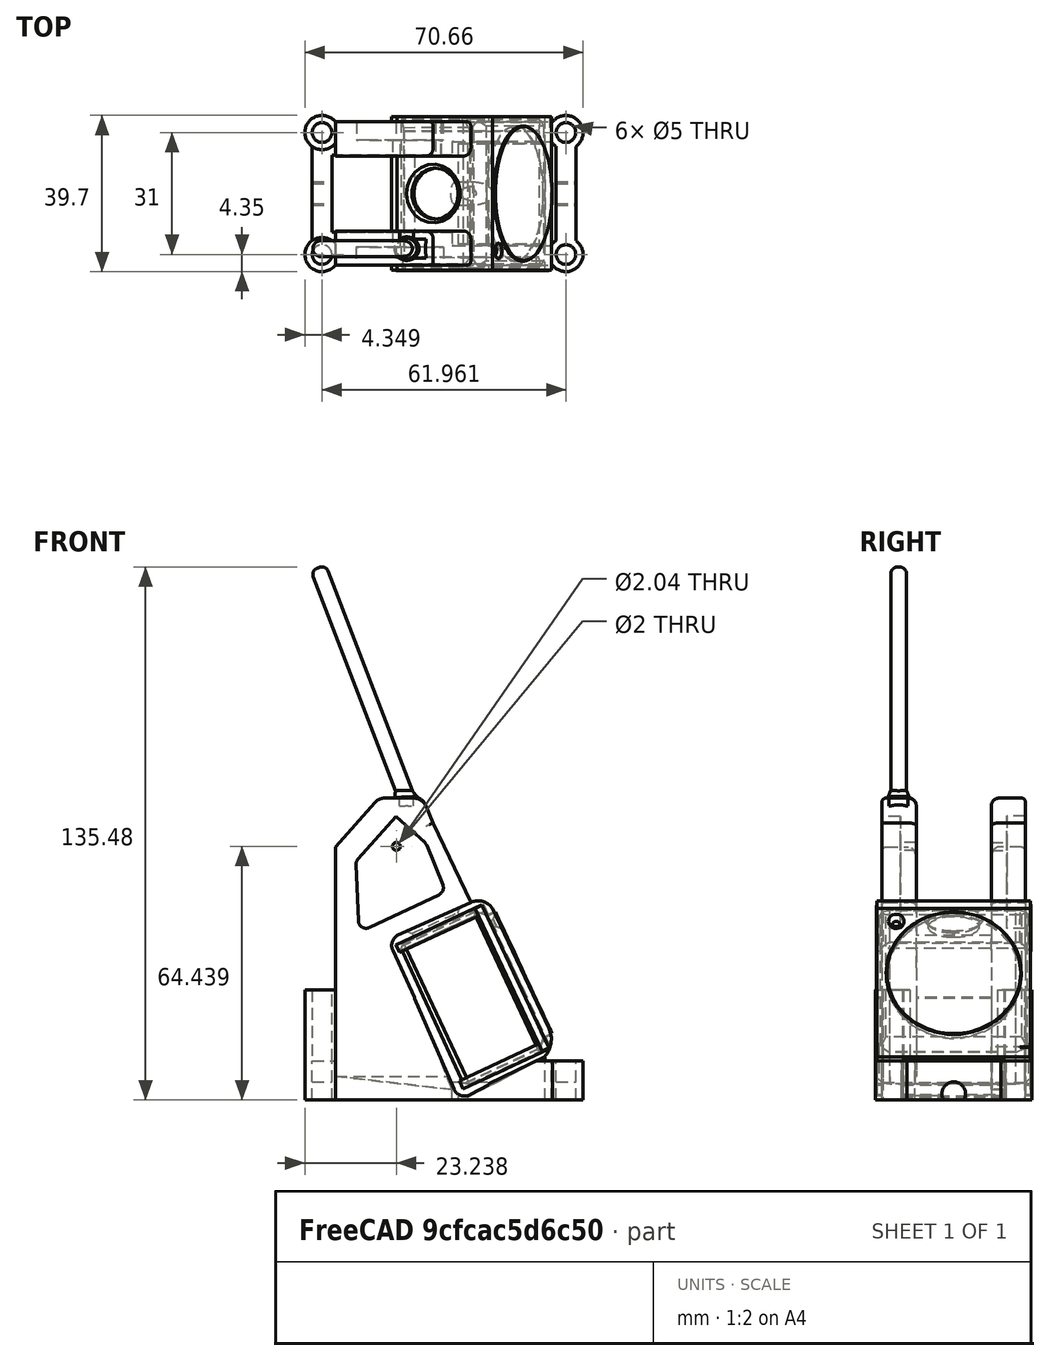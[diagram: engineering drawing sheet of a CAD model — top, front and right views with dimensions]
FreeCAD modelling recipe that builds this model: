
FCSTD DOCUMENT  (FreeCAD 0.19R24267 +99 (Git))
Label: fr7狗坐
License: All rights reserved
LicenseURL: http://en.wikipedia.org/wiki/All_rights_reserved
objects: Sketcher::SketchObject×14, PartDesign::Pad×10, Part::Fillet×6, Part::Cylinder×4, PartDesign::Pocket×4, Part::Cut×4, PartDesign::Body×4, Part::Chamfer×3, Part::Box×3, Part::MultiFuse×3, Mesh::Feature×2, PartDesign::Chamfer×1, Part::Fuse×1, App::MeasureDistance×1
note: 72 computed .brp shape members not serialized (recipe doc carries the construction recipe); baked Part::Feature solids carry a one-line shape summary decoded from their .brp

FEATURE [Sketcher::SketchObject] Sketch
  FullyConstrained = false
  MapMode = 5
  Support = -> [XY_Plane]
  sketch-geometry (30):
    g0: Circle CenterX=-30.9806 CenterY=15.5 CenterZ=0 NormalX=0 NormalY=0 NormalZ=1 AngleXU=0 Radius=2.5
    g1: Circle CenterX=-30.9806 CenterY=-15.5 CenterZ=0 NormalX=0 NormalY=0 NormalZ=1 AngleXU=0 Radius=2.5
    g2: LineSegment StartX=-30.9806 StartY=15.5 StartZ=0 EndX=-30.9806 EndY=-15.5 EndZ=0
    g3: ArcOfCircle CenterX=-30.9806 CenterY=15.5 CenterZ=0 NormalX=0 NormalY=0 NormalZ=1 AngleXU=0 Radius=4.35 StartAngle=5.32464 EndAngle=5.73271
    g4: ArcOfCircle CenterX=-30.9806 CenterY=-15.5 CenterZ=0 NormalX=0 NormalY=0 NormalZ=1 AngleXU=0 Radius=4.35 StartAngle=2.18305 EndAngle=5.60634
    g5: LineSegment StartX=-33.4806 StartY=11.9402 StartZ=0 EndX=-33.4806 EndY=-11.9402 EndZ=0
    g6: LineSegment StartX=-28.4806 StartY=11.9402 StartZ=0 EndX=-28.4806 EndY=-11.9402 EndZ=0
    g7: GeomPoint X=0.092343 Y=18.2246 Z=0
    g8: GeomPoint X=0 Y=13.2246 Z=0
    g9: LineSegment StartX=0.092343 StartY=18.2246 StartZ=0 EndX=-27.5895 EndY=18.2246 EndZ=0
    g10: LineSegment StartX=0 StartY=13.2246 StartZ=0 EndX=-27.2732 EndY=13.2246 EndZ=0
    g11: LineSegment StartX=-0.092343 StartY=-18.2246 StartZ=0 EndX=-27.5895 EndY=-18.2246 EndZ=0
    g12: LineSegment StartX=0 StartY=-13.2246 StartZ=0 EndX=-27.2732 EndY=-13.2246 EndZ=0
    g13: ArcOfCircle CenterX=-30.9806 CenterY=15.5 CenterZ=0 NormalX=0 NormalY=0 NormalZ=1 AngleXU=0 Radius=4.35 StartAngle=0.676845 EndAngle=4.10014
    g14: ArcOfCircle CenterX=-30.9806 CenterY=-15.5 CenterZ=0 NormalX=0 NormalY=0 NormalZ=1 AngleXU=0 Radius=4.35 StartAngle=0.550471 EndAngle=0.958543
    g15: Circle CenterX=30.9806 CenterY=15.5 CenterZ=0 NormalX=0 NormalY=0 NormalZ=1 AngleXU=0 Radius=2.5
    g16: Circle CenterX=30.9806 CenterY=-15.5 CenterZ=0 NormalX=0 NormalY=0 NormalZ=1 AngleXU=0 Radius=2.5
    g17: LineSegment StartX=30.9806 StartY=15.5 StartZ=0 EndX=30.9806 EndY=-15.5 EndZ=0
    g18: ArcOfCircle CenterX=30.9806 CenterY=15.5 CenterZ=0 NormalX=0 NormalY=0 NormalZ=1 AngleXU=0 Radius=4.35 StartAngle=3.69206 EndAngle=4.10014
    g19: ArcOfCircle CenterX=30.9806 CenterY=-15.5 CenterZ=0 NormalX=0 NormalY=0 NormalZ=1 AngleXU=0 Radius=4.35 StartAngle=3.81844 EndAngle=7.24173
    g20: LineSegment StartX=33.4806 StartY=11.9402 StartZ=0 EndX=33.4806 EndY=-11.9402 EndZ=0
    g21: LineSegment StartX=28.4806 StartY=11.9402 StartZ=0 EndX=28.4806 EndY=-11.9402 EndZ=0
    g22: GeomPoint X=0.092343 Y=18.2246 Z=0
    g23: GeomPoint X=0 Y=13.2246 Z=0
    g24: LineSegment StartX=0.092343 StartY=18.2246 StartZ=0 EndX=27.5895 EndY=18.2246 EndZ=0
    g25: LineSegment StartX=0 StartY=13.2246 StartZ=0 EndX=27.2732 EndY=13.2246 EndZ=0
    g26: LineSegment StartX=-0.092343 StartY=-18.2246 StartZ=0 EndX=27.5895 EndY=-18.2246 EndZ=0
    g27: LineSegment StartX=0 StartY=-13.2246 StartZ=0 EndX=27.2732 EndY=-13.2246 EndZ=0
    g28: ArcOfCircle CenterX=30.9806 CenterY=15.5 CenterZ=0 NormalX=0 NormalY=0 NormalZ=1 AngleXU=0 Radius=4.35 StartAngle=5.32464 EndAngle=8.74793
    g29: ArcOfCircle CenterX=30.9806 CenterY=-15.5 CenterZ=0 NormalX=0 NormalY=0 NormalZ=1 AngleXU=0 Radius=4.35 StartAngle=2.18305 EndAngle=2.59112
  constraints (67):
    c: Coincident(g2,g0)
    c: Coincident(g2,g1)
    c: Symmetric(g0,g1,g-1)
    c: Distance(g2) = 31
    c: Diameter(g1) = 5
    c: Equal(g0,g1)
    c: Coincident(g3,g0)
    c: Coincident(g4,g1)
    c: Equal(g3,g4)
    c: Diameter(g3) = 8.7
    c: Vertical(g5)
    c: Vertical(g6)
    c: Symmetric(g5,g6,g2)
    c: Distance(g5,g6) = 5
    c: PointOnObject(g8,g-2)
    c: Coincident(g9,g7)
    c: Horizontal(g9)
    c: Coincident(g10,g8)
    c: Horizontal(g10)
    c: DistanceX(g0) = -30.9806
    c: Distance(g9,g10) = 5
    c: Horizontal(g11)
    c: Horizontal(g12)
    c: Coincident(g3,g6)
    c: Coincident(g13,g5)
    c: Coincident(g4,g5)
    c: Coincident(g14,g6)
    c: Coincident(g3,g10)
    c: Coincident(g13,g9)
    c: Coincident(g3,g13)
    c: Equal(g4,g14)
    c: PointOnObject(g4,g11)
    c: PointOnObject(g14,g12)
    c: Coincident(g4,g14)
    c: Coincident(g17,g15)
    c: Coincident(g17,g16)
    c: Distance(g17) = 31
    c: Diameter(g16) = 5
    c: Equal(g15,g16)
    c: Coincident(g18,g15)
    c: Coincident(g19,g16)
    c: Equal(g18,g19)
    c: Diameter(g18) = 8.7
    c: Vertical(g20)
    c: Vertical(g21)
    c: Symmetric(g20,g21,g17)
    c: Distance(g20,g21) = 5
    c: Coincident(g24,g22)
    c: Horizontal(g24)
    c: Coincident(g25,g23)
    c: Horizontal(g25)
    c: Distance(g24,g25) = 5
    c: Horizontal(g26)
    c: Horizontal(g27)
    c: Coincident(g18,g21)
    c: Coincident(g28,g20)
    c: Coincident(g19,g20)
    c: Coincident(g29,g21)
    c: Coincident(g18,g25)
    c: Coincident(g28,g24)
    c: Coincident(g18,g28)
    c: Equal(g19,g29)
    c: PointOnObject(g19,g26)
    c: PointOnObject(g29,g27)
    c: Coincident(g19,g29)
    c: Coincident(g24,g9)
    c: Coincident(g11,g26)
FEATURE [PartDesign::Pad] Pad
  Direction = (1,1,1)
  Length = 10
  Length2 = 100
  Profile = -> Sketch
  Type = 0
FEATURE [Sketcher::SketchObject] Sketch001
  ExternalGeometry = -> [Pad]
  FullyConstrained = true
  MapMode = 5
  Placement = pos=(0,0,10) rot=(0,0,1;0rad)
  Support = -> [Pad]
  sketch-geometry (4):
    g0: Circle CenterX=-30.9806 CenterY=15.5 CenterZ=0 NormalX=0 NormalY=0 NormalZ=1 AngleXU=0 Radius=4.35
    g1: Circle CenterX=-30.9806 CenterY=-15.5 CenterZ=0 NormalX=0 NormalY=0 NormalZ=1 AngleXU=0 Radius=4.35
    g2: Circle CenterX=-30.9806 CenterY=15.5 CenterZ=0 NormalX=0 NormalY=0 NormalZ=1 AngleXU=0 Radius=2.5
    g3: Circle CenterX=-30.9806 CenterY=-15.5 CenterZ=0 NormalX=0 NormalY=0 NormalZ=1 AngleXU=0 Radius=2.5
  constraints (8):
    c: Coincident(g0,g-3)
    c: PointOnObject(g-3,g0)
    c: Coincident(g1,g-4)
    c: PointOnObject(g-4,g1)
    c: Coincident(g2,g0)
    c: Coincident(g3,g1)
    c: Equal(g2,g-6)
    c: Equal(g-5,g3)
FEATURE [PartDesign::Pad] Pad001
  BaseFeature = -> Pad
  Direction = (1,1,1)
  Length = 18
  Length2 = 100
  Profile = -> Sketch001
  Type = 0
FEATURE [Sketcher::SketchObject] Sketch002
  ExternalGeometry = -> [Pad001]
  FullyConstrained = false
  MapMode = 5
  Placement = pos=(0,-18.2246,0) rot=(1,0,0;1.5708rad)
  Support = -> [Pad001]
  sketch-geometry (10):
    g0: LineSegment StartX=-27.5895 StartY=33.6278 StartZ=0 EndX=-27.5895 EndY=6.05961 EndZ=0
    g1: LineSegment StartX=-27.5895 StartY=6.05961 StartZ=0 EndX=2.28396 EndY=6.05961 EndZ=0
    g2: LineSegment StartX=2.28396 StartY=6.05961 StartZ=0 EndX=-12.4012 EndY=39.5723 EndZ=0
    g3: LineSegment StartX=-27.5895 StartY=33.6278 StartZ=0 EndX=-27.6022 EndY=64.3335 EndZ=0
    g4: LineSegment StartX=-27.6022 StartY=64.3335 StartZ=0 EndX=-16.5842 EndY=76.7241 EndZ=0
    g5: LineSegment StartX=-16.5842 StartY=76.7241 StartZ=0 EndX=-5.41744 EndY=76.7241 EndZ=0
    g6: LineSegment StartX=-5.41744 StartY=76.7241 StartZ=0 EndX=-2.75155 EndY=70.4171 EndZ=0
    g7: LineSegment StartX=-2.75155 StartY=70.4171 StartZ=0 EndX=7.1536 EndY=49.4808 EndZ=0
    g8: LineSegment StartX=7.1536 StartY=49.4808 StartZ=0 EndX=-12.4012 EndY=39.5723 EndZ=0
    g9: Circle CenterX=-12.092 CenterY=64.4385 CenterZ=0 NormalX=0 NormalY=0 NormalZ=1 AngleXU=0 Radius=1
  constraints (15):
    c: Vertical(g0)
    c: Coincident(g0,g1)
    c: Horizontal(g1)
    c: Coincident(g1,g2)
    c: PointOnObject(g0,g-3)
    c: Coincident(g0,g3)
    c: Coincident(g3,g4)
    c: Coincident(g4,g5)
    c: Horizontal(g5)
    c: Coincident(g5,g6)
    c: Coincident(g6,g7)
    c: Coincident(g7,g8)
    c: Coincident(g2,g8)
    c: Diameter(g9) = 2
    c: Distance(g9,g7) = 11
FEATURE [Mesh::Feature] DJIaction2
  Placement = pos=(8.54836,-0.15952,23.2121) rot=(-0.211541,-0.211541,0.954201;1.61766rad)
FEATURE [Sketcher::SketchObject] Sketch004
  FullyConstrained = false
  MapMode = 5
  Placement = pos=(0,0,0) rot=(0.57735,0.57735,0.57735;2.0944rad)
  sketch-geometry (20):
    g0: GeomPoint X=-11.8779 Y=-12.6655 Z=0
    g1: GeomPoint X=-0.108248 Y=-18.7716 Z=0
    g2: LineSegment StartX=-24.6153 StartY=-40.6455 StartZ=0 EndX=-24.6153 EndY=-11.9915 EndZ=0
    g3: LineSegment StartX=-24.6153 StartY=-11.9915 StartZ=0 EndX=-30.1099 EndY=-0.0706558 EndZ=0
    g4: ArcOfCircle CenterX=-27.3854 CenterY=1.18515 CenterZ=0 NormalX=0 NormalY=0 NormalZ=1 AngleXU=0 Radius=3 StartAngle=2.15583 EndAngle=3.5735
    g5: LineSegment StartX=-29.0421 StartY=3.68622 StartZ=0 EndX=-10.214 EndY=12.1607 EndZ=0
    g6: ArcOfCircle CenterX=-8.43551 CenterY=8.20941 CenterZ=0 NormalX=0 NormalY=0 NormalZ=1 AngleXU=0 Radius=4.33313 StartAngle=0.572968 EndAngle=1.99373
    g7: LineSegment StartX=-4.79441 StartY=10.5585 StartZ=0 EndX=9.54356 EndY=-19.8682 EndZ=0
    g8: ArcOfCircle CenterX=3.63879 CenterY=-22.6507 CenterZ=0 NormalX=0 NormalY=0 NormalZ=1 AngleXU=0 Radius=6.52753 StartAngle=5.53634 EndAngle=6.72355
    g9: LineSegment StartX=8.42894 StartY=-27.085 StartZ=0 EndX=-5.79484 EndY=-34.0458 EndZ=0
    g10: LineSegment StartX=-5.79484 StartY=-34.0458 StartZ=0 EndX=-5.79484 EndY=-40.6455 EndZ=0
    g11: LineSegment StartX=-5.79484 StartY=-40.6455 StartZ=0 EndX=-24.6153 EndY=-40.6455 EndZ=0
    g12: LineSegment StartX=-27.9814 StartY=0.422502 StartZ=0 EndX=-27.4298 EndY=1.92854 EndZ=0
    g13: LineSegment StartX=-27.4298 StartY=1.92854 StartZ=0 EndX=-9.86172 EndY=10.0842 EndZ=0
    g14: LineSegment StartX=-9.86172 StartY=10.0842 StartZ=0 EndX=-6.40235 EndY=8.97087 EndZ=0
    g15: LineSegment StartX=-6.40235 StartY=8.97087 StartZ=0 EndX=8.11905 EndY=-22.1001 EndZ=0
    g16: LineSegment StartX=8.11905 StartY=-22.1001 StartZ=0 EndX=7.08521 EndY=-25.9571 EndZ=0
    g17: LineSegment StartX=7.08521 StartY=-25.9571 StartZ=0 EndX=-10.3747 EndY=-34.1479 EndZ=0
    g18: LineSegment StartX=-10.3747 StartY=-34.1479 StartZ=0 EndX=-12.2539 EndY=-33.7769 EndZ=0
    g19: LineSegment StartX=-12.2539 StartY=-33.7769 StartZ=0 EndX=-27.9814 EndY=0.422502 EndZ=0
  constraints (22):
    c: Vertical(g2)
    c: Coincident(g2,g3)
    c: Tangent(g3,g4) = 1.5708
    c: Coincident(g4,g5)
    c: Tangent(g5,g6) = 1.5708
    c: Coincident(g6,g7)
    c: Tangent(g7,g8) = 1.5708
    c: Coincident(g8,g9)
    c: Coincident(g9,g10)
    c: Vertical(g10)
    c: Coincident(g10,g11)
    c: Coincident(g11,g2)
    c: Horizontal(g11)
    c: Radius(g4) = 3
    c: Coincident(g12,g13)
    c: Coincident(g13,g14)
    c: Coincident(g14,g15)
    c: Coincident(g15,g16)
    c: Coincident(g16,g17)
    c: Coincident(g17,g18)
    c: Coincident(g18,g19)
    c: Coincident(g19,g12)
FEATURE [Part::Cylinder] Cylinder  label="圆柱体"
  Angle = 360
  AttacherType = Attacher::AttachEngine3D
  Height = 10
  Placement = pos=(14.6,-10.5408,3.91178) rot=(-1,0,0;1.13446rad)
  Radius = 1
FEATURE [PartDesign::Pad] Pad004
  Direction = (1,1,1)
  Length = 39
  Length2 = 100
  Midplane = true
  Placement = pos=(0,0,0) rot=(0.57735,0.57735,0.57735;2.0944rad)
  Profile = -> Sketch004
  Type = 0
FEATURE [Sketcher::SketchObject] Sketch006
  FullyConstrained = false
  MapMode = 5
  Placement = pos=(19.5,-4.3e-15,4.3e-15) rot=(0.57735,0.57735,0.57735;2.0944rad)
  Support = -> [Pad004]
  sketch-geometry (6):
    g0: LineSegment StartX=-24.8415 StartY=-11.7709 StartZ=0 EndX=-14.5728 EndY=-35.3199 EndZ=0
    g1: ArcOfCircle CenterX=-11.8655 CenterY=-34.1393 CenterZ=0 NormalX=0 NormalY=0 NormalZ=1 AngleXU=0 Radius=2.95356 StartAngle=3.55279 EndAngle=5.24992
    g2: LineSegment StartX=-10.3532 StartY=-36.6764 StartZ=0 EndX=-4.86179 EndY=-33.6672 EndZ=0
    g3: LineSegment StartX=-4.86179 StartY=-33.6672 StartZ=0 EndX=-4.86179 EndY=-40.8624 EndZ=0
    g4: LineSegment StartX=-4.86179 StartY=-40.8624 StartZ=0 EndX=-24.8415 EndY=-40.8624 EndZ=0
    g5: LineSegment StartX=-24.8415 StartY=-40.8624 StartZ=0 EndX=-24.8415 EndY=-11.7709 EndZ=0
  constraints (9):
    c: Tangent(g0,g1) = -1.5708
    c: Coincident(g1,g2)
    c: Coincident(g2,g3)
    c: Vertical(g3)
    c: Coincident(g3,g4)
    c: Horizontal(g4)
    c: Coincident(g4,g5)
    c: Coincident(g5,g0)
    c: Vertical(g5)
FEATURE [PartDesign::Pocket] Pocket
  BaseFeature = -> Pad004
  Length = 42
  Length2 = 100
  Placement = pos=(0,0,0) rot=(0.57735,0.57735,0.57735;2.0944rad)
  Profile = -> Sketch006
  Type = 0
FEATURE [Sketcher::SketchObject] Sketch005
  FullyConstrained = false
  MapMode = 5
  Placement = pos=(2.3e-15,-6.27212,13.935) rot=(0.205419,0.205419,-0.956873;1.61487rad)
  Support = -> [Pocket]
  sketch-geometry (1):
    g0: Circle CenterX=14.8131 CenterY=0.011856 CenterZ=0 NormalX=0 NormalY=0 NormalZ=1 AngleXU=0 Radius=6.44328
FEATURE [PartDesign::Pocket] Pocket001
  BaseFeature = -> Pocket
  Length = 5
  Length2 = 100
  Placement = pos=(0,0,0) rot=(0.57735,0.57735,0.57735;2.0944rad)
  Profile = -> Sketch005
  Type = 0
FEATURE [Sketcher::SketchObject] Sketch007
  FullyConstrained = false
  MapMode = 5
  Placement = pos=(0,0.148179,0.0698264) rot=(-0.472141,-0.472141,-0.744423;1.86175rad)
  Support = -> [Pocket001]
  sketch-geometry (1):
    g0: Circle CenterX=-6.53962 CenterY=0 CenterZ=0 NormalX=0 NormalY=0 NormalZ=1 AngleXU=0 Radius=17.1695
  constraints (1):
    c: PointOnObject(g0,g-1)
FEATURE [PartDesign::Pocket] Pocket002
  BaseFeature = -> Pocket001
  Length = 5
  Length2 = 100
  Placement = pos=(0,0,0) rot=(0.57735,0.57735,0.57735;2.0944rad)
  Profile = -> Sketch007
  Type = 0
FEATURE [Sketcher::SketchObject] Sketch008
  FullyConstrained = false
  MapMode = 5
  Placement = pos=(-4e-15,11.2586,-23.9993) rot=(0.212592,0.212592,-0.953734;1.61815rad)
  Support = -> [Pocket002]
  sketch-geometry (8):
    g0: LineSegment StartX=1.91594 StartY=19.5973 StartZ=0 EndX=3.84524 EndY=19.5973 EndZ=0
    g1: LineSegment StartX=3.84524 StartY=19.5973 StartZ=0 EndX=3.84524 EndY=18.6619 EndZ=0
    g2: LineSegment StartX=3.84524 StartY=18.6619 StartZ=0 EndX=1.91594 EndY=17.1286 EndZ=0
    g3: LineSegment StartX=1.91594 StartY=17.1286 StartZ=0 EndX=1.91594 EndY=19.5973 EndZ=0
    g4: LineSegment StartX=1.51851 StartY=-16.7716 StartZ=0 EndX=3.74988 EndY=-18.7373 EndZ=0
    g5: LineSegment StartX=3.74988 StartY=-18.7373 StartZ=0 EndX=3.74988 EndY=-19.5199 EndZ=0
    g6: LineSegment StartX=3.74988 StartY=-19.5199 StartZ=0 EndX=1.51851 EndY=-19.5093 EndZ=0
    g7: LineSegment StartX=1.51851 StartY=-19.5093 StartZ=0 EndX=1.51851 EndY=-16.7716 EndZ=0
  constraints (13):
    c: Horizontal(g0)
    c: Coincident(g0,g1)
    c: Vertical(g1)
    c: Coincident(g1,g2)
    c: Coincident(g2,g3)
    c: Coincident(g3,g0)
    c: Vertical(g3)
    c: Coincident(g4,g5)
    c: Vertical(g5)
    c: Coincident(g5,g6)
    c: Coincident(g6,g7)
    c: Coincident(g7,g4)
    c: Vertical(g7)
FEATURE [PartDesign::Pad] Pad005
  BaseFeature = -> Pocket002
  Direction = (1,1,1)
  Length = 40
  Length2 = 100
  Placement = pos=(0,0,0) rot=(0.57735,0.57735,0.57735;2.0944rad)
  Profile = -> Sketch008
  Type = 0
FEATURE [Sketcher::SketchObject] Sketch009
  FullyConstrained = false
  MapMode = 5
  Placement = pos=(-1e-16,-1.81357,-0.847593) rot=(0.644815,0.644815,-0.4104;2.36271rad)
  Support = -> [Pad005]
  sketch-geometry (20):
    g0: LineSegment StartX=-13.5866 StartY=19.5377 StartZ=0 EndX=-11.4604 EndY=19.5377 EndZ=0
    g1: LineSegment StartX=-11.4604 StartY=19.5377 StartZ=0 EndX=-11.4604 EndY=18.9559 EndZ=0
    g2: LineSegment StartX=-11.4604 StartY=18.9559 StartZ=0 EndX=-12.6134 EndY=17.9404 EndZ=0
    g3: LineSegment StartX=-12.6134 StartY=17.9404 StartZ=0 EndX=-13.5866 EndY=15.7824 EndZ=0
    g4: LineSegment StartX=-13.5866 StartY=15.7824 StartZ=0 EndX=-13.5866 EndY=19.5377 EndZ=0
    g5: LineSegment StartX=24.4522 StartY=19.5683 StartZ=0 EndX=24.4522 EndY=19.0297 EndZ=0
    g6: LineSegment StartX=24.4522 StartY=19.0297 StartZ=0 EndX=25.6188 EndY=17.9888 EndZ=0
    g7: LineSegment StartX=25.6188 StartY=17.9888 StartZ=0 EndX=26.7559 EndY=15.8493 EndZ=0
    g8: LineSegment StartX=26.7559 StartY=15.8493 StartZ=0 EndX=26.7559 EndY=19.5597 EndZ=0
    g9: LineSegment StartX=26.7559 StartY=19.5597 StartZ=0 EndX=24.4522 EndY=19.5683 EndZ=0
    g10: LineSegment StartX=-13.772 StartY=-16.0866 StartZ=0 EndX=-12.642 EndY=-18.0406 EndZ=0
    g11: LineSegment StartX=-12.642 StartY=-18.0406 StartZ=0 EndX=-11.7945 EndY=-18.8882 EndZ=0
    g12: LineSegment StartX=-11.7945 StartY=-18.8882 StartZ=0 EndX=-11.818 EndY=-19.5474 EndZ=0
    g13: LineSegment StartX=-11.818 StartY=-19.5474 StartZ=0 EndX=-13.772 EndY=-19.5474 EndZ=0
    g14: LineSegment StartX=-13.772 StartY=-19.5474 StartZ=0 EndX=-13.772 EndY=-16.0866 EndZ=0
    g15: LineSegment StartX=26.956 StartY=-14.6143 StartZ=0 EndX=25.7566 EndY=-17.9599 EndZ=0
    g16: LineSegment StartX=25.7566 StartY=-17.9599 StartZ=0 EndX=24.5099 EndY=-18.9856 EndZ=0
    g17: LineSegment StartX=24.5099 StartY=-18.9856 StartZ=0 EndX=24.5099 EndY=-19.5853 EndZ=0
    g18: LineSegment StartX=24.5099 StartY=-19.5853 StartZ=0 EndX=26.956 EndY=-19.5853 EndZ=0
    g19: LineSegment StartX=26.956 StartY=-19.5853 StartZ=0 EndX=26.956 EndY=-14.6143 EndZ=0
  constraints (30):
    c: Horizontal(g0)
    c: Coincident(g0,g1)
    c: Vertical(g1)
    c: Coincident(g1,g2)
    c: Coincident(g2,g3)
    c: Coincident(g3,g4)
    c: Coincident(g4,g0)
    c: Vertical(g4)
    c: Vertical(g5)
    c: Coincident(g5,g6)
    c: Coincident(g6,g7)
    c: Coincident(g7,g8)
    c: Vertical(g8)
    c: Coincident(g8,g9)
    c: Coincident(g9,g5)
    c: Coincident(g10,g11)
    c: Coincident(g11,g12)
    c: Coincident(g12,g13)
    c: Horizontal(g13)
    c: Coincident(g13,g14)
    c: Coincident(g14,g10)
    c: Vertical(g14)
    c: Coincident(g15,g16)
    c: Coincident(g16,g17)
    c: Vertical(g17)
    c: Coincident(g17,g18)
    c: Horizontal(g18)
    c: Coincident(g18,g19)
    c: Coincident(g19,g15)
    c: Vertical(g19)
FEATURE [PartDesign::Pad] Pad006
  BaseFeature = -> Pad005
  Direction = (1,1,1)
  Length = 24
  Length2 = 100
  Placement = pos=(0,0,0) rot=(0.57735,0.57735,0.57735;2.0944rad)
  Profile = -> Sketch009
  Type = 0
FEATURE [PartDesign::Chamfer] Chamfer
  Angle = 45
  Base = -> Pad006 [Edge112]
  BaseFeature = -> Pad006
  ChamferType = 0
  FlipDirection = false
  Placement = pos=(0,0,0) rot=(0.57735,0.57735,0.57735;2.0944rad)
  Size = 1
  Size2 = 1
  SupportTransform = false
FEATURE [Part::Cut] Cut001
  Base = -> Chamfer
  Tool = -> Cylinder
FEATURE [Part::Chamfer] Chamfer001
  Base = -> Cut001
  Edges = 1 edges r=1: [Edge116]
  Placement = pos=(17.1,-8e-15,38.1) rot=(0,0,-1;1.5708rad)
FEATURE [PartDesign::Pad] Pad007
  BaseFeature = -> Pad001
  Direction = (1,1,1)
  Length = 8.7
  Length2 = 100
  Profile = -> Sketch002
  Reversed = true
  Type = 0
FEATURE [Sketcher::SketchObject] Sketch010
  ExternalGeometry = -> [Pad007]
  FullyConstrained = false
  MapMode = 5
  Placement = pos=(0,18.2246,0) rot=(0,0.707107,0.707107;3.14159rad)
  Support = -> [Pad007]
  sketch-geometry (10):
    g0: LineSegment StartX=-2.01273 StartY=2.66899 StartZ=0 EndX=12.1947 EndY=39.6769 EndZ=0
    g1: LineSegment StartX=12.1947 StartY=39.6769 StartZ=0 EndX=-7.1536 EndY=49.4808 EndZ=0
    g2: LineSegment StartX=-7.1536 StartY=49.4808 StartZ=0 EndX=2.75155 EndY=70.4171 EndZ=0
    g3: LineSegment StartX=2.75155 StartY=70.4171 StartZ=0 EndX=5.41744 EndY=76.7241 EndZ=0
    g4: LineSegment StartX=5.41744 StartY=76.7241 StartZ=0 EndX=16.5842 EndY=76.7241 EndZ=0
    g5: LineSegment StartX=16.5842 StartY=76.7241 StartZ=0 EndX=27.6022 EndY=64.3335 EndZ=0
    g6: LineSegment StartX=27.6022 StartY=64.3335 StartZ=0 EndX=27.5895 EndY=33.6278 EndZ=0
    g7: LineSegment StartX=27.5895 StartY=33.6278 StartZ=0 EndX=27.5895 EndY=6.05961 EndZ=0
    g8: LineSegment StartX=27.5895 StartY=6.05961 StartZ=0 EndX=-2.01273 EndY=2.66899 EndZ=0
    g9: Circle CenterX=12.092 CenterY=64.4385 CenterZ=0 NormalX=0 NormalY=0 NormalZ=1 AngleXU=0 Radius=1.01766
  constraints (18):
    c: PointOnObject(g0,g-7)
    c: Coincident(g0,g1)
    c: Coincident(g1,g-7)
    c: Coincident(g1,g2)
    c: Coincident(g2,g-3)
    c: Coincident(g2,g3)
    c: Coincident(g3,g-4)
    c: Coincident(g3,g4)
    c: Coincident(g4,g-5)
    c: Coincident(g4,g5)
    c: Coincident(g5,g-6)
    c: Coincident(g5,g6)
    c: Coincident(g6,g-8)
    c: Coincident(g6,g7)
    c: Coincident(g7,g-8)
    c: Coincident(g7,g8)
    c: Coincident(g8,g0)
    c: Coincident(g9,g-9)
FEATURE [PartDesign::Pad] Pad008
  BaseFeature = -> Pad007
  Direction = (1,1,1)
  Length = 8.7
  Length2 = 100
  Profile = -> Sketch010
  Reversed = true
  Type = 0
FEATURE [Sketcher::SketchObject] Sketch011
  FullyConstrained = false
  MapMode = 5
  Placement = pos=(0,-18.2246,0) rot=(1,0,0;1.5708rad)
  Support = -> [Pad008]
  sketch-geometry (3):
    g0: LineSegment StartX=0.833711 StartY=11.4687 StartZ=0 EndX=4.50931 EndY=2.00599 EndZ=0
    g1: LineSegment StartX=4.50931 StartY=2.00599 StartZ=0 EndX=23.8258 EndY=11.4687 EndZ=0
    g2: LineSegment StartX=23.8258 StartY=11.4687 StartZ=0 EndX=0.833711 EndY=11.4687 EndZ=0
  constraints (4):
    c: Coincident(g0,g1)
    c: Coincident(g1,g2)
    c: Coincident(g2,g0)
    c: Horizontal(g2)
FEATURE [PartDesign::Pocket] Pocket003
  BaseFeature = -> Pad008
  Length = 54
  Length2 = 100
  Profile = -> Sketch011
  Type = 0
FEATURE [PartDesign::Body] Body
  Group = -> [Sketch,Pad,Sketch001,Pad001,Sketch002,Pad007,Sketch010,Pad008,Sketch011,Pocket003]
  Origin = -> Origin
  Tip = -> Pocket003
FEATURE [Part::Fuse] Fusion
  Base = -> Body
  Tool = -> Chamfer001
FEATURE [Part::Box] Box  label="立方体"
  AttacherType = Attacher::AttachEngine3D
  Height = 10
  Length = 31
  Placement = pos=(-29,-13.8,0) rot=(0,0,1;0rad)
  Width = 4
FEATURE [Part::Box] Box001  label="立方体001"
  AttacherType = Attacher::AttachEngine3D
  Height = 10
  Length = 31
  Placement = pos=(-29,9.7,0) rot=(0,0,1;0rad)
  Width = 4
FEATURE [Part::Cylinder] Cylinder001  label="圆柱体001"
  Angle = 360
  AttacherType = Attacher::AttachEngine3D
  Height = 88
  Placement = pos=(-46.6,0,1.6) rot=(0,1,0;1.5708rad)
  Radius = 3
FEATURE [Part::MultiFuse] Fusion001
  Shapes = -> [Fusion,Box,Box001]
FEATURE [Part::Cut] Cut
  Base = -> Fusion001
  Tool = -> Cylinder001
FEATURE [Sketcher::SketchObject] Sketch012
  FullyConstrained = false
  MapMode = 5
  Placement = pos=(0,0,0) rot=(1,0,0;1.5708rad)
  Support = -> [XZ_Plane001]
  sketch-geometry (5):
    g0: LineSegment StartX=-22.3043 StartY=60.6667 StartZ=0 EndX=-21.6797 EndY=42.4858 EndZ=0
    g1: LineSegment StartX=-21.6797 StartY=42.4858 StartZ=0 EndX=0.342644 EndY=53.0117 EndZ=0
    g2: LineSegment StartX=0.342644 StartY=53.0117 StartZ=0 EndX=-4.61541 EndY=65.1345 EndZ=0
    g3: LineSegment StartX=-4.61541 StartY=65.1345 StartZ=0 EndX=-12.1485 EndY=72.1584 EndZ=0
    g4: LineSegment StartX=-12.1485 StartY=72.1584 StartZ=0 EndX=-22.3043 EndY=60.6667 EndZ=0
  constraints (5):
    c: Coincident(g1,g2)
    c: Coincident(g2,g3)
    c: Coincident(g3,g4)
    c: Coincident(g4,g0)
    c: Coincident(g0,g1)
FEATURE [PartDesign::Pad] Pad009
  Direction = (1,1,1)
  Length = 5
  Length2 = 100
  Placement = pos=(0,0,0) rot=(1,0,0;1.5708rad)
  Profile = -> Sketch012
  Type = 0
FEATURE [PartDesign::Body] Body001
  Group = -> [Sketch012,Pad009]
  Origin = -> Origin001
  Placement = pos=(0,18.5,0) rot=(0,0,1;0rad)
  Tip = -> Pad009
FEATURE [Sketcher::SketchObject] Sketch013
  FullyConstrained = false
  MapMode = 5
  Placement = pos=(0,0,0) rot=(1,0,0;1.5708rad)
  Support = -> [XZ_Plane002]
  sketch-geometry (5):
    g0: LineSegment StartX=-22.3825 StartY=60.6311 StartZ=0 EndX=-21.6479 EndY=42.5445 EndZ=0
    g1: LineSegment StartX=-21.6479 StartY=42.5445 StartZ=0 EndX=0.410162 EndY=52.9282 EndZ=0
    g2: LineSegment StartX=0.410162 StartY=52.9282 StartZ=0 EndX=-4.5407 EndY=65.1103 EndZ=0
    g3: LineSegment StartX=-4.5407 StartY=65.1103 StartZ=0 EndX=-12.2299 EndY=72.0529 EndZ=0
    g4: LineSegment StartX=-12.2299 StartY=72.0529 StartZ=0 EndX=-22.3825 EndY=60.6311 EndZ=0
  constraints (4):
    c: Coincident(g1,g2)
    c: Coincident(g2,g3)
    c: Coincident(g3,g4)
    c: Coincident(g1,g0)
FEATURE [PartDesign::Pad] Pad010
  Direction = (1,1,1)
  Length = 5
  Length2 = 100
  Placement = pos=(0,0,0) rot=(1,0,0;1.5708rad)
  Profile = -> Sketch013
  Type = 0
FEATURE [PartDesign::Body] Body002
  Group = -> [Sketch013,Pad010]
  Origin = -> Origin002
  Placement = pos=(0,-13.6,0) rot=(0,0,1;0rad)
  Tip = -> Pad010
FEATURE [Part::Cut] Cut002
  Base = -> Cut
  Tool = -> Body001
FEATURE [Part::Cut] Cut003
  Base = -> Cut002
  Tool = -> Body002
FEATURE [Part::Cylinder] Cylinder002  label="圆柱体002"
  Angle = 360
  AttacherType = Attacher::AttachEngine3D
  Height = 2.5
  Placement = pos=(17.9984,0,31.2784) rot=(0,1,0;1.13446rad)
  Radius = 17
FEATURE [Mesh::Feature] Unnamed_FR7___DJI_Hero8_FlatUpright_DoubleScrew_r2_v10  label="Unnamed-FR7_-_DJI_Hero8_FlatUpright_DoubleScrew_r2 v10"
FEATURE [Sketcher::SketchObject] Sketch014
  FullyConstrained = false
  MapMode = 5
  Placement = pos=(0,0,0) rot=(1,0,0;1.5708rad)
  Support = -> [XZ_Plane003]
  sketch-geometry (5):
    g0: LineSegment StartX=25.6988 StartY=10.8533 StartZ=0 EndX=5.96536 EndY=0.693796 EndZ=0
    g1: LineSegment StartX=5.96536 StartY=0.693796 StartZ=0 EndX=3.60905 EndY=0.988336 EndZ=0
    g2: LineSegment StartX=3.60905 StartY=0.988336 StartZ=0 EndX=3.60905 EndY=0 EndZ=0
    g3: LineSegment StartX=3.60905 StartY=0 StartZ=0 EndX=25.6988 EndY=0 EndZ=0
    g4: LineSegment StartX=25.6988 StartY=0 StartZ=0 EndX=25.6988 EndY=10.8533 EndZ=0
  constraints (9):
    c: Coincident(g0,g1)
    c: Coincident(g1,g2)
    c: PointOnObject(g2,g-1)
    c: Vertical(g2)
    c: Coincident(g2,g3)
    c: PointOnObject(g3,g-1)
    c: Coincident(g3,g4)
    c: Coincident(g4,g0)
    c: Vertical(g4)
FEATURE [PartDesign::Pad] Pad011
  Direction = (1,1,1)
  Length = 25.5
  Length2 = 100
  Placement = pos=(0,0,0) rot=(1,0,0;1.5708rad)
  Profile = -> Sketch014
  Type = 0
FEATURE [PartDesign::Body] Body003
  Group = -> [Sketch014,Pad011]
  Origin = -> Origin003
  Placement = pos=(0,12.7,0) rot=(0,0,1;0rad)
  Tip = -> Pad011
FEATURE [Part::Box] Box009  label="立方体009"
  AttacherType = Attacher::AttachEngine3D
  Height = 39.5
  Length = 32
  Placement = pos=(6.48567,15.8,4.04964) rot=(0.211541,-0.211541,-0.954201;1.61766rad)
  Width = 19.5
FEATURE [App::MeasureDistance] Distance  label="Distance: 39.92 mm"
  Distance = 39.9201
  P1 = (-10.2032,16.798,40.0873)
  P2 = (6.8973,15.6775,4.03279)
FEATURE [Part::MultiFuse] Fusion002
  Shapes = -> [Cut003,Cylinder002,Body003,Box009]
FEATURE [Part::Cylinder] Cylinder003  label="圆柱体003"
  Angle = 360
  AttacherType = Attacher::AttachEngine3D
  Height = 64
  Placement = pos=(-8.99,-14,75.48) rot=(0,-1,0;0.366519rad)
  Radius = 2
FEATURE [Part::MultiFuse] Fusion003
  Shapes = -> [Fusion002,Cylinder003]
FEATURE [Part::Chamfer] Chamfer002
  Base = -> Fusion003
  Edges = 1 edges r=1: [Edge2]
FEATURE [Part::Chamfer] Chamfer003
  Base = -> Chamfer002
  Edges = 1 edges r=1: [Edge3]
FEATURE [Part::Fillet] Fillet
  Base = -> Chamfer003
  Edges = 1 edges r=1.6: [Edge2]
FEATURE [Part::Fillet] Fillet001
  Base = -> Fillet
  Edges = 4 edges r=3.3: [Edge10,Edge12,Edge419,Edge420]
FEATURE [Part::Fillet] Fillet002
  Base = -> Fillet001
  Edges = 2 edges r=2: [Edge51,Edge226]
FEATURE [Part::Fillet] Fillet003
  Base = -> Fillet002
  Edges = 2 edges r=1: [Edge37,Edge204]
FEATURE [Part::Fillet] Fillet004
  Base = -> Fillet003
  Edges = 4 edges r=2: [Edge127,Edge128,Edge130,Edge134]
FEATURE [Part::Fillet] Fillet005
  Base = -> Fillet004
  Edges = 4 edges r=2: [Edge476,Edge478,Edge479,Edge483]
